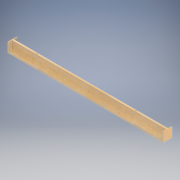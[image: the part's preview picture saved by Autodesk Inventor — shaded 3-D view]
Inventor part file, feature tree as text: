
AUTODESK INVENTOR PART (.ipt)
format: ipt  version: 2022.2 (Build 262287010, 287A)  size: 187,904 bytes
history: native  units: in
note: dims shown in document units (in); Inventor stores cm internally (conversion verified against a paired STEP export)
features: direct_edit x1, extrude x1, sketch x1, projected_geometry x1, revolve x1
ambient origin geometry x8: Origin, YZ Plane, XZ Plane, XY Plane, X Axis, Y Axis, Z Axis, Center Point
bodies: Solid1 (feature_tree), Body1 (feature_tree)
feature tree (5):
  direct_edit  "Direct Edit1"
  extrude  "Extrusion1"  Depth=1.0in TaperAngle=0.0deg
  sketch  "Sketch1"  dims[d0=180.0deg d1=1.0in d2=0.0in]
  projected_geometry  "Projected Loop1"
  revolve  "Rotate1"  [1 undecoded]
note: 1 required parameter value undecoded (feature->parameter linkage not recoverable at this tier; creation-order binding heuristic only, values carry confidence <= 0.55)
